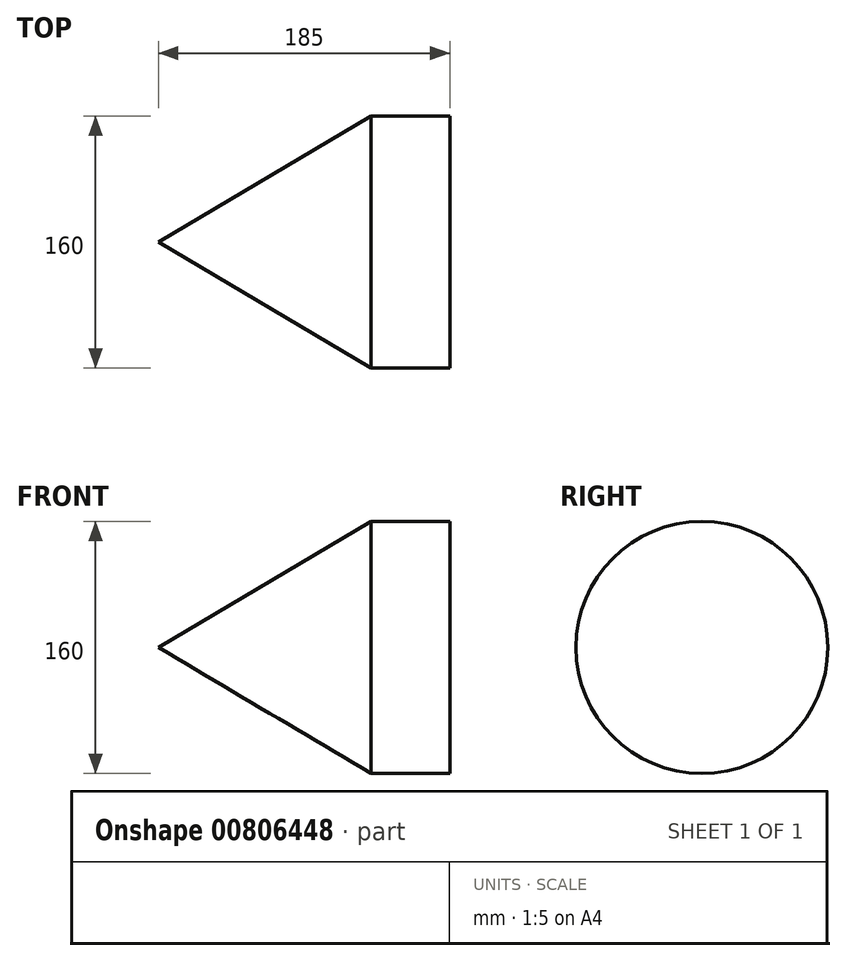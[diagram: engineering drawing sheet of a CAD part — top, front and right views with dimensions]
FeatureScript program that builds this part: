
annotation { "Feature Type Name" : "Feature", "Feature Type Description" : "" }
export const myFeature = defineFeature(function(context is Context, id is Id, definition is map)
    precondition{}
    {
        {
            var Q0;
            Q0=qCreatedBy(makeId("Front.planeOp"),FACE);
            var sketch = newSketch(context, id + "F0", { "sketchPlane" : qUnion([Q0])});
            skLineSegment(sketch, "E0", {"start": v(0, 0) * mm, "end": v(0, 80) * mm});
            skLineSegment(sketch, "E1", {"start": v(0, 0) * mm, "end": v(-185, 0) * mm});
            skLineSegment(sketch, "E2", {"start": v(0, 80) * mm, "end": v(-50, 80) * mm});
            skLineSegment(sketch, "E3", {"start": v(-50, 80) * mm, "end": v(-185, 0) * mm});
            skSolve(sketch);
        }
        {
            var Q0;
            Q0=qSketchRegion(id+"F0",true);
            var Q1;
            Q1=sQuery(id+"F0.wireOp",EDGE,"E1");
            revolve(context, id + "F1", {"surfaceOperationType" : NewSurfaceOperationType.NEW, "entities" : qUnion([Q0]), "axis" : qUnion([Q1]), "revolveType" : RevolveType.FULL});
        }
    });
